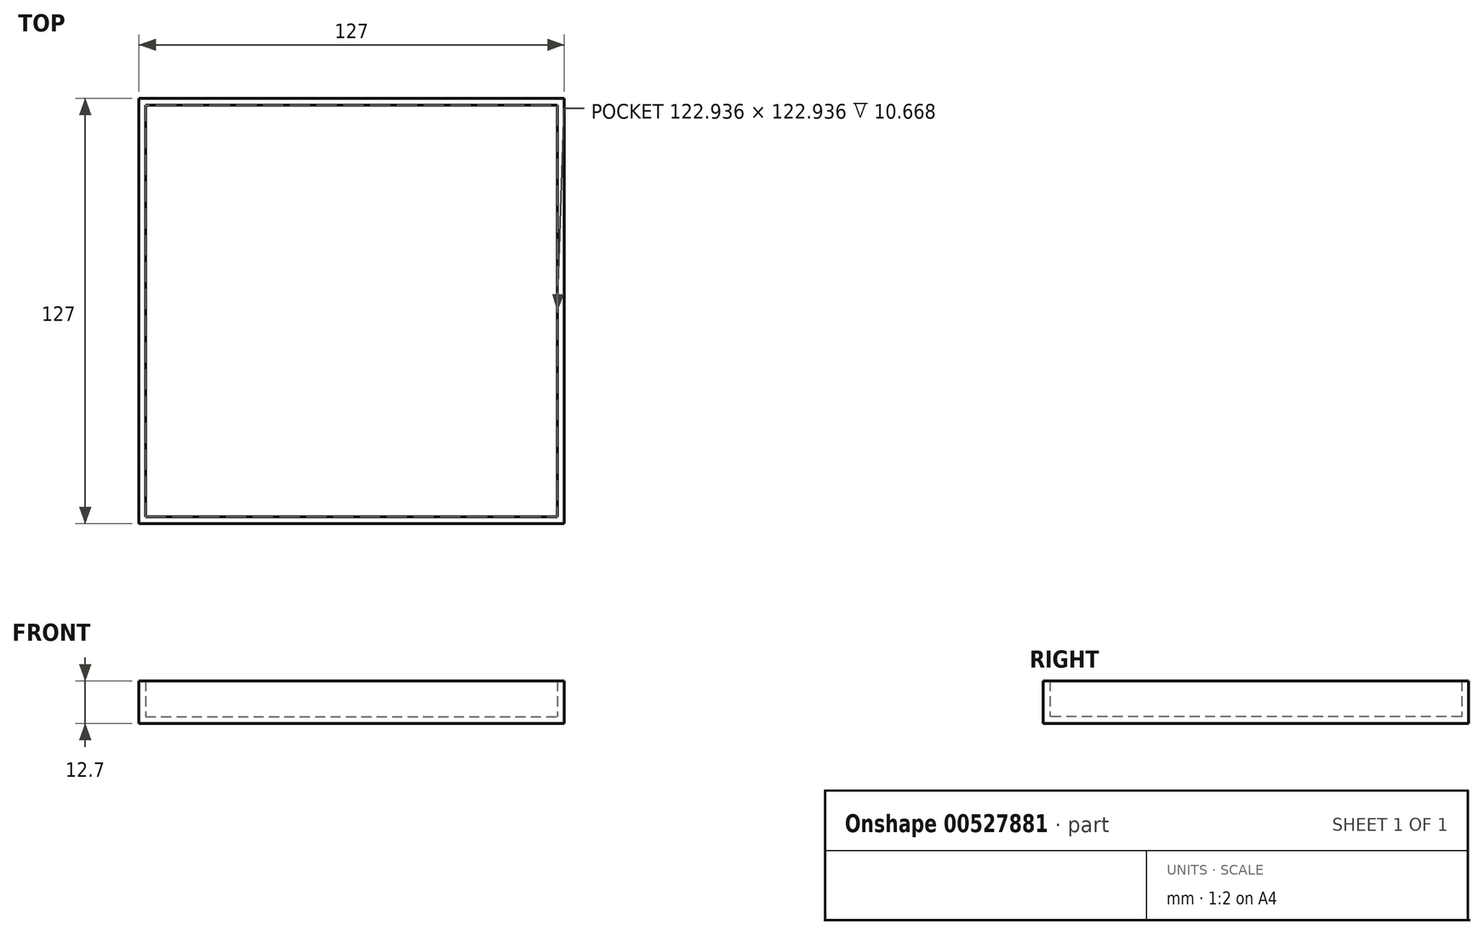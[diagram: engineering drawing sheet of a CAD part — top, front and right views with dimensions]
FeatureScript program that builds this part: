
annotation { "Feature Type Name" : "Feature", "Feature Type Description" : "" }
export const myFeature = defineFeature(function(context is Context, id is Id, definition is map)
    precondition{}
    {
        {
            var Q0;
            Q0=qCreatedBy(makeId("Top.planeOp"),FACE);
            var sketch = newSketch(context, id + "F0", { "sketchPlane" : qUnion([Q0])});
            skLineSegment(sketch, "E0.bottom", {"start": v(0, 0) * mm, "end": v(127, 0) * mm});
            skLineSegment(sketch, "E0.top", {"start": v(0, -127) * mm, "end": v(127, -127) * mm});
            skLineSegment(sketch, "E0.left", {"start": v(0, 0) * mm, "end": v(0, -127) * mm});
            skLineSegment(sketch, "E0.right", {"start": v(127, 0) * mm, "end": v(127, -127) * mm});
            skLineSegment(sketch, "E1.bottom", {"start": v(2.03, -2.03) * mm, "end": v(124.97, -2.03) * mm});
            skLineSegment(sketch, "E1.top", {"start": v(2.03, -124.97) * mm, "end": v(124.97, -124.97) * mm});
            skLineSegment(sketch, "E1.left", {"start": v(2.03, -2.03) * mm, "end": v(2.03, -124.97) * mm});
            skLineSegment(sketch, "E1.right", {"start": v(124.97, -2.03) * mm, "end": v(124.97, -124.97) * mm});
            skLineSegment(sketch, "E2", {"start": v(2.03, -2.03) * mm, "end": v(2.03, 0) * mm, "construction": true});
            skLineSegment(sketch, "E3", {"start": v(2.03, -2.03) * mm, "end": v(0, -2.03) * mm, "construction": true});
            skLineSegment(sketch, "E4", {"start": v(124.97, -124.97) * mm, "end": v(127, -124.97) * mm, "construction": true});
            skLineSegment(sketch, "E5", {"start": v(124.97, -124.97) * mm, "end": v(124.97, -127) * mm, "construction": true});
            skSolve(sketch);
        }
        {
            var Q0;
            Q0=makeQuery(id+"F0.imprint","IMPRINT",FACE,{"disambiguationData":[TD([[makeQuery(id+"F0.imprint","IMPRINT",EDGE,{"derivedFrom":sQuery(id+"F0.wireOp",EDGE,"E1.bottom")}),-1.0]])]});
            extrude(context, id + "F1", {"entities" : qUnion([Q0]), "depth" : 2.03 * mm, "offsetDistance" : 25.4 * mm});
        }
        {
            var Q0;
            Q0=makeQuery(id+"F0.imprint","IMPRINT",FACE,{"disambiguationData":[TD([[makeQuery(id+"F0.imprint","IMPRINT",EDGE,{"derivedFrom":sQuery(id+"F0.wireOp",EDGE,"E0.bottom")}),-1.0]])]});
            extrude(context, id + "F2", {"entities" : qUnion([Q0]), "operationType" : NewBodyOperationType.ADD, "depth" : 12.7 * mm, "offsetDistance" : 25.4 * mm});
        }
    });
